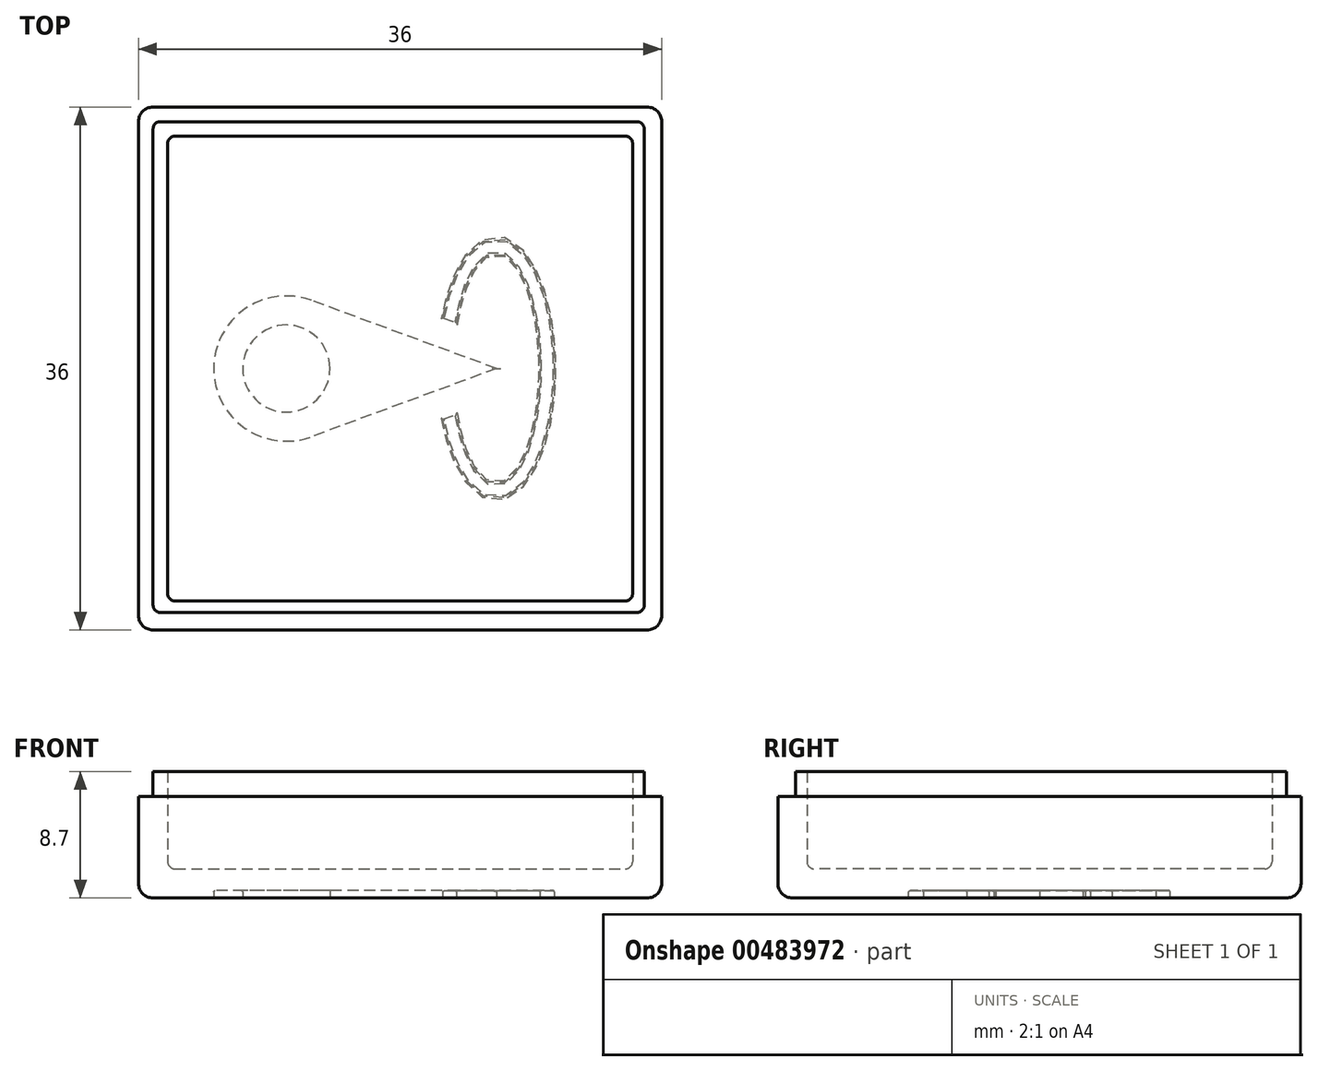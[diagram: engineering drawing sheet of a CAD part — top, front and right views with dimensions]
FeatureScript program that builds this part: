
annotation { "Feature Type Name" : "Feature", "Feature Type Description" : "" }
export const myFeature = defineFeature(function(context is Context, id is Id, definition is map)
    precondition{}
    {
        {
            var Q0;
            Q0=qCreatedBy(makeId("Top.planeOp"),FACE);
            var sketch = newSketch(context, id + "F0", { "sketchPlane" : qUnion([Q0])});
            skLineSegment(sketch, "E0.bottom", {"start": v(-17, 17) * mm, "end": v(16.8, 17) * mm});
            skLineSegment(sketch, "E0.top", {"start": v(-17, -16.8) * mm, "end": v(16.8, -16.8) * mm});
            skLineSegment(sketch, "E0.left", {"start": v(-17, 17) * mm, "end": v(-17, -16.8) * mm});
            skLineSegment(sketch, "E0.right", {"start": v(16.8, 17) * mm, "end": v(16.8, -16.8) * mm});
            skLineSegment(sketch, "E1.bottom", {"start": v(-18.9, 18.9) * mm, "end": v(19.1, 18.9) * mm});
            skLineSegment(sketch, "E1.top", {"start": v(-18.9, -19.1) * mm, "end": v(19.1, -19.1) * mm});
            skLineSegment(sketch, "E1.left", {"start": v(-18.9, 18.9) * mm, "end": v(-18.9, -19.1) * mm});
            skLineSegment(sketch, "E1.right", {"start": v(19.1, 18.9) * mm, "end": v(19.1, -19.1) * mm});
            skSolve(sketch);
        }
        {
            var Q0;
            Q0=qCreatedBy(makeId("Top.planeOp"),FACE);
            var sketch = newSketch(context, id + "F1", { "sketchPlane" : qUnion([Q0])});
            skLineSegment(sketch, "E2.bottom", {"start": v(-18, 18) * mm, "end": v(18, 18) * mm});
            skLineSegment(sketch, "E2.top", {"start": v(-18, -18) * mm, "end": v(18, -18) * mm});
            skLineSegment(sketch, "E2.left", {"start": v(-18, 18) * mm, "end": v(-18, -18) * mm});
            skLineSegment(sketch, "E2.right", {"start": v(18, 18) * mm, "end": v(18, -18) * mm});
            skSolve(sketch);
        }
        {
            var Q0;
            Q0=makeQuery(id+"F1.imprint","IMPRINT",FACE,{"disambiguationData":[TD([[makeQuery(id+"F1.imprint","IMPRINT",EDGE,{"derivedFrom":sQuery(id+"F1.wireOp",EDGE,"E2.bottom")}),-1.0]])]});
            extrude(context, id + "F2", {"entities" : qUnion([Q0]), "depth" : 8.7 * mm});
        }
        {
            var Q0;
            Q0=makeQuery(id+"F2.opExtrude","CAP_FACE",FACE,{"disambiguationData":[OSD([sQuery(id+"F1.wireOp",EDGE,"E2.bottom"),sQuery(id+"F1.wireOp",EDGE,"E2.top"),sQuery(id+"F1.wireOp",EDGE,"E2.left"),sQuery(id+"F1.wireOp",EDGE,"E2.right")])],"isStart":false});
            shell(context, id + "F3", {"entities" : qUnion([Q0]), "thickness" : 2 * mm});
        }
        {
            var Q0;
            Q0=makeQuery(id+"F2.opExtrude","CAP_EDGE",EDGE,{"disambiguationData":[OSD([sQuery(id+"F1.wireOp",EDGE,"E2.right")])],"isStart":true});
            var Q1;
            Q1=makeQuery(id+"F2.opExtrude","CAP_EDGE",EDGE,{"disambiguationData":[OSD([sQuery(id+"F1.wireOp",EDGE,"E2.bottom")])],"isStart":true});
            var Q2;
            Q2=makeQuery(id+"F2.opExtrude","CAP_EDGE",EDGE,{"disambiguationData":[OSD([sQuery(id+"F1.wireOp",EDGE,"E2.left")])],"isStart":true});
            var Q3;
            Q3=makeQuery(id+"F2.opExtrude","CAP_EDGE",EDGE,{"disambiguationData":[OSD([sQuery(id+"F1.wireOp",EDGE,"E2.top")])],"isStart":true});
            fillet(context, id + "F4", {"entities" : qUnion([Q0, Q1, Q2, Q3]), "radius" : 1 * mm, "tangentPropagation" : true, "allowEdgeOverflow" : false});
        }
        {
            var Q0;
            Q0 = qSketchRegion(id + "F0", true);
            extrude(context, id + "F5", {"entities" : qUnion([Q0]), "operationType" : NewBodyOperationType.REMOVE, "depth" : 10 * mm, "hasSecondDirection" : true, "secondDirectionOppositeDirection" : false, "secondDirectionDepth" : 7 * mm});
        }
        {
            var Q0;
            Q0=qCreatedBy(makeId("Top.planeOp"),FACE);
            var sketch = newSketch(context, id + "F6", { "sketchPlane" : qUnion([Q0])});
            skArc(sketch, "E3", {"start": v(-6.1, 4.7) * mm, "mid": v(-12.83, 0) * mm, "end": v(-6.1, -4.7) * mm});
            skLineSegment(sketch, "E4", {"start": v(6.62, 0) * mm, "end": v(-6.1, 4.7) * mm});
            skLineSegment(sketch, "E5", {"start": v(6.62, 0) * mm, "end": v(-6.1, -4.7) * mm});
            skCircle(sketch, "E6", {"center": v(-7.83, 0) * mm, "radius": 3 * mm});
            skEllipticalArc(sketch, "E7", {});
            skEllipticalArc(sketch, "E8", {});
            skLineSegment(sketch, "E9", {"start": v(2.94, 3.5) * mm, "end": v(3.87, 3.15) * mm});
            skPoint(sketch, "E9.endSnap0", {"position": v(0.26, 2.35) * mm});
            skLineSegment(sketch, "E10", {"start": v(2.94, -3.5) * mm, "end": v(3.87, -3.15) * mm});
            skPoint(sketch, "E11.orphan", {"position": v(6.04, 2.35) * mm});
            const initialGuessF6  = {"E7": [0.006624625995755196, 0, 0, -1, 0.009, 0.004, 5.110756187143681, 4.314021773625698], "E8": [0.006624625995755196, 0, 0, -1, 0.008, 0.003, 5.1169157867029655, 4.307862174066413]};
            skSetInitialGuess(sketch, initialGuessF6);
            skSolve(sketch);
        }
        {
            var Q0;
            Q0 = qSketchRegion(id + "F6", true);
            extrude(context, id + "F7", {"entities" : qUnion([Q0]), "operationType" : NewBodyOperationType.REMOVE, "depth" : 0.5 * mm});
        }
        {
            var Q0;
            Q0=makeQuery(id+"F7.boolean.opBoolean","COPY",EDGE,{"derivedFrom":makeQuery(id+"F7.opExtrude","CAP_EDGE",EDGE,{"disambiguationData":[OSD([sQuery(id+"F6.wireOp",EDGE,"E3")])],"isStart":false})});
            var Q1;
            Q1=makeQuery(id+"F7.boolean.opBoolean","COPY",EDGE,{"derivedFrom":makeQuery(id+"F7.opExtrude","CAP_EDGE",EDGE,{"disambiguationData":[OSD([sQuery(id+"F6.wireOp",EDGE,"E5")])],"isStart":false})});
            var Q2;
            Q2=makeQuery(id+"F7.boolean.opBoolean","COPY",EDGE,{"derivedFrom":makeQuery(id+"F7.opExtrude","CAP_EDGE",EDGE,{"disambiguationData":[OSD([sQuery(id+"F6.wireOp",EDGE,"E4")])],"isStart":false})});
            var Q3;
            Q3=makeQuery(id+"F7.boolean.opBoolean","COPY",EDGE,{"derivedFrom":makeQuery(id+"F7.opExtrude","CAP_EDGE",EDGE,{"disambiguationData":[OSD([sQuery(id+"F6.wireOp",EDGE,"E3")])],"isStart":true})});
            var Q4;
            Q4=makeQuery(id+"F7.boolean.opBoolean","COPY",EDGE,{"derivedFrom":makeQuery(id+"F7.opExtrude","CAP_EDGE",EDGE,{"disambiguationData":[OSD([sQuery(id+"F6.wireOp",EDGE,"E4")])],"isStart":true})});
            var Q5;
            Q5=makeQuery(id+"F7.boolean.opBoolean","COPY",EDGE,{"derivedFrom":makeQuery(id+"F7.opExtrude","CAP_EDGE",EDGE,{"disambiguationData":[OSD([sQuery(id+"F6.wireOp",EDGE,"E5")])],"isStart":true})});
            var Q6;
            Q6=makeQuery(id+"F7.boolean.opBoolean","COPY",EDGE,{"derivedFrom":makeQuery(id+"F7.opExtrude","CAP_EDGE",EDGE,{"disambiguationData":[OSD([sQuery(id+"F6.wireOp",EDGE,"E6")])],"isStart":false})});
            var Q7;
            Q7=makeQuery(id+"F7.boolean.opBoolean","COPY",EDGE,{"derivedFrom":makeQuery(id+"F7.opExtrude","CAP_EDGE",EDGE,{"disambiguationData":[OSD([sQuery(id+"F6.wireOp",EDGE,"E6")])],"isStart":true})});
            var Q8;
            Q8=makeQuery(id+"F7.boolean.opBoolean","COPY",EDGE,{"derivedFrom":makeQuery(id+"F7.opExtrude","CAP_EDGE",EDGE,{"disambiguationData":[OSD([sQuery(id+"F6.wireOp",EDGE,"E8")])],"isStart":false})});
            var Q9;
            Q9=makeQuery(id+"F7.boolean.opBoolean","COPY",EDGE,{"derivedFrom":makeQuery(id+"F7.opExtrude","CAP_EDGE",EDGE,{"disambiguationData":[OSD([sQuery(id+"F6.wireOp",EDGE,"E10")])],"isStart":false})});
            var Q10;
            Q10=makeQuery(id+"F7.boolean.opBoolean","COPY",EDGE,{"derivedFrom":makeQuery(id+"F7.opExtrude","CAP_EDGE",EDGE,{"disambiguationData":[OSD([sQuery(id+"F6.wireOp",EDGE,"E7")])],"isStart":false})});
            var Q11;
            Q11=makeQuery(id+"F7.boolean.opBoolean","COPY",EDGE,{"derivedFrom":makeQuery(id+"F7.opExtrude","CAP_EDGE",EDGE,{"disambiguationData":[OSD([sQuery(id+"F6.wireOp",EDGE,"E9")])],"isStart":false})});
            var Q12;
            Q12=makeQuery(id+"F7.boolean.opBoolean","COPY",EDGE,{"derivedFrom":makeQuery(id+"F7.opExtrude","CAP_EDGE",EDGE,{"disambiguationData":[OSD([sQuery(id+"F6.wireOp",EDGE,"E9")])],"isStart":true})});
            var Q13;
            Q13=makeQuery(id+"F7.boolean.opBoolean","COPY",EDGE,{"derivedFrom":makeQuery(id+"F7.opExtrude","CAP_EDGE",EDGE,{"disambiguationData":[OSD([sQuery(id+"F6.wireOp",EDGE,"E8")])],"isStart":true})});
            var Q14;
            Q14=makeQuery(id+"F7.boolean.opBoolean","COPY",EDGE,{"derivedFrom":makeQuery(id+"F7.opExtrude","CAP_EDGE",EDGE,{"disambiguationData":[OSD([sQuery(id+"F6.wireOp",EDGE,"E7")])],"isStart":true})});
            var Q15;
            Q15=makeQuery(id+"F7.boolean.opBoolean","COPY",EDGE,{"derivedFrom":makeQuery(id+"F7.opExtrude","CAP_EDGE",EDGE,{"disambiguationData":[OSD([sQuery(id+"F6.wireOp",EDGE,"E10")])],"isStart":true})});
            fillet(context, id + "F8", {"entities" : qUnion([Q0, Q1, Q2, Q3, Q4, Q5, Q6, Q7, Q8, Q9, Q10, Q11, Q12, Q13, Q14, Q15]), "radius" : 0.1 * mm, "tangentPropagation" : true, "allowEdgeOverflow" : false});
        }
        {
            var Q0;
            Q0=makeQuery(id+"F3.opShell","OFFSET_FACE",FACE,{"disambiguationData":[OSD([sQuery(id+"F1.wireOp",EDGE,"E2.bottom"),sQuery(id+"F1.wireOp",EDGE,"E2.top"),sQuery(id+"F1.wireOp",EDGE,"E2.left"),sQuery(id+"F1.wireOp",EDGE,"E2.right")])]});
            var Q1;
            Q1=makeQuery(id+"F3.opShell","OFFSET_EDGE",EDGE,{"disambiguationData":[OSD([sQuery(id+"F1.wireOp",EDGE,"E2.top"),sQuery(id+"F1.wireOp",EDGE,"E2.right")])]});
            var Q2;
            Q2=makeQuery(id+"F3.opShell","OFFSET_EDGE",EDGE,{"disambiguationData":[OSD([sQuery(id+"F1.wireOp",EDGE,"E2.bottom"),sQuery(id+"F1.wireOp",EDGE,"E2.right")])]});
            var Q3;
            Q3=makeQuery(id+"F3.opShell","OFFSET_EDGE",EDGE,{"disambiguationData":[OSD([sQuery(id+"F1.wireOp",EDGE,"E2.bottom"),sQuery(id+"F1.wireOp",EDGE,"E2.left")])]});
            var Q4;
            Q4=makeQuery(id+"F3.opShell","OFFSET_EDGE",EDGE,{"disambiguationData":[OSD([sQuery(id+"F1.wireOp",EDGE,"E2.top"),sQuery(id+"F1.wireOp",EDGE,"E2.left")])]});
            var Q5;
            Q5=makeQuery(id+"F5.boolean.opBoolean","COPY",EDGE,{"derivedFrom":makeQuery(id+"F5.opExtrude","SWEPT_EDGE",EDGE,{"disambiguationData":[OSD([sQuery(id+"F0.wireOp",EDGE,"E0.top"),sQuery(id+"F0.wireOp",EDGE,"E0.right")])]})});
            var Q6;
            Q6=makeQuery(id+"F5.boolean.opBoolean","COPY",EDGE,{"derivedFrom":makeQuery(id+"F5.opExtrude","SWEPT_EDGE",EDGE,{"disambiguationData":[OSD([sQuery(id+"F0.wireOp",EDGE,"E0.top"),sQuery(id+"F0.wireOp",EDGE,"E0.left")])]})});
            var Q7;
            Q7=makeQuery(id+"F5.boolean.opBoolean","COPY",EDGE,{"derivedFrom":makeQuery(id+"F5.opExtrude","SWEPT_EDGE",EDGE,{"disambiguationData":[OSD([sQuery(id+"F0.wireOp",EDGE,"E0.bottom"),sQuery(id+"F0.wireOp",EDGE,"E0.left")])]})});
            var Q8;
            Q8=makeQuery(id+"F5.boolean.opBoolean","COPY",EDGE,{"derivedFrom":makeQuery(id+"F5.opExtrude","SWEPT_EDGE",EDGE,{"disambiguationData":[OSD([sQuery(id+"F0.wireOp",EDGE,"E0.bottom"),sQuery(id+"F0.wireOp",EDGE,"E0.right")])]})});
            fillet(context, id + "F9", {"entities" : qUnion([Q0, Q1, Q2, Q3, Q4, Q5, Q6, Q7, Q8]), "radius" : 0.5 * mm, "tangentPropagation" : true, "allowEdgeOverflow" : false});
        }
        {
            var Q0;
            Q0=makeQuery(id+"F2.opExtrude","SWEPT_EDGE",EDGE,{"disambiguationData":[OSD([sQuery(id+"F1.wireOp",EDGE,"E2.bottom"),sQuery(id+"F1.wireOp",EDGE,"E2.left")])]});
            var Q1;
            Q1=makeQuery(id+"F2.opExtrude","SWEPT_EDGE",EDGE,{"disambiguationData":[OSD([sQuery(id+"F1.wireOp",EDGE,"E2.bottom"),sQuery(id+"F1.wireOp",EDGE,"E2.right")])]});
            var Q2;
            Q2=makeQuery(id+"F2.opExtrude","SWEPT_EDGE",EDGE,{"disambiguationData":[OSD([sQuery(id+"F1.wireOp",EDGE,"E2.top"),sQuery(id+"F1.wireOp",EDGE,"E2.left")])]});
            var Q3;
            Q3=makeQuery(id+"F2.opExtrude","SWEPT_EDGE",EDGE,{"disambiguationData":[OSD([sQuery(id+"F1.wireOp",EDGE,"E2.top"),sQuery(id+"F1.wireOp",EDGE,"E2.right")])]});
            fillet(context, id + "F10", {"entities" : qUnion([Q0, Q1, Q2, Q3]), "radius" : 1 * mm, "tangentPropagation" : true, "allowEdgeOverflow" : false});
        }
    });
